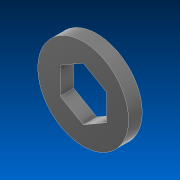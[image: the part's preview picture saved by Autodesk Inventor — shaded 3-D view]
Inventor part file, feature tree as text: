
AUTODESK INVENTOR PART (.ipt)
format: ipt  version: 2022.2 (Build 262287000, 287)  size: 94,208 bytes
history: native  units: in
note: dims shown in document units (in); Inventor stores cm internally (conversion verified against a paired STEP export)
features: extrude x1, sketch x1
ambient origin geometry x8: Origin, YZ Plane, XZ Plane, XY Plane, X Axis, Y Axis, Z Axis, Center Point
bodies: Solid1 (feature_tree)
feature tree (2):
  extrude  "Extrusion1"  Depth=0.15in
  sketch  "Sketch1"  dims[d0=0.51in d1=1.0in d2=0.15in d3=0.0in]
